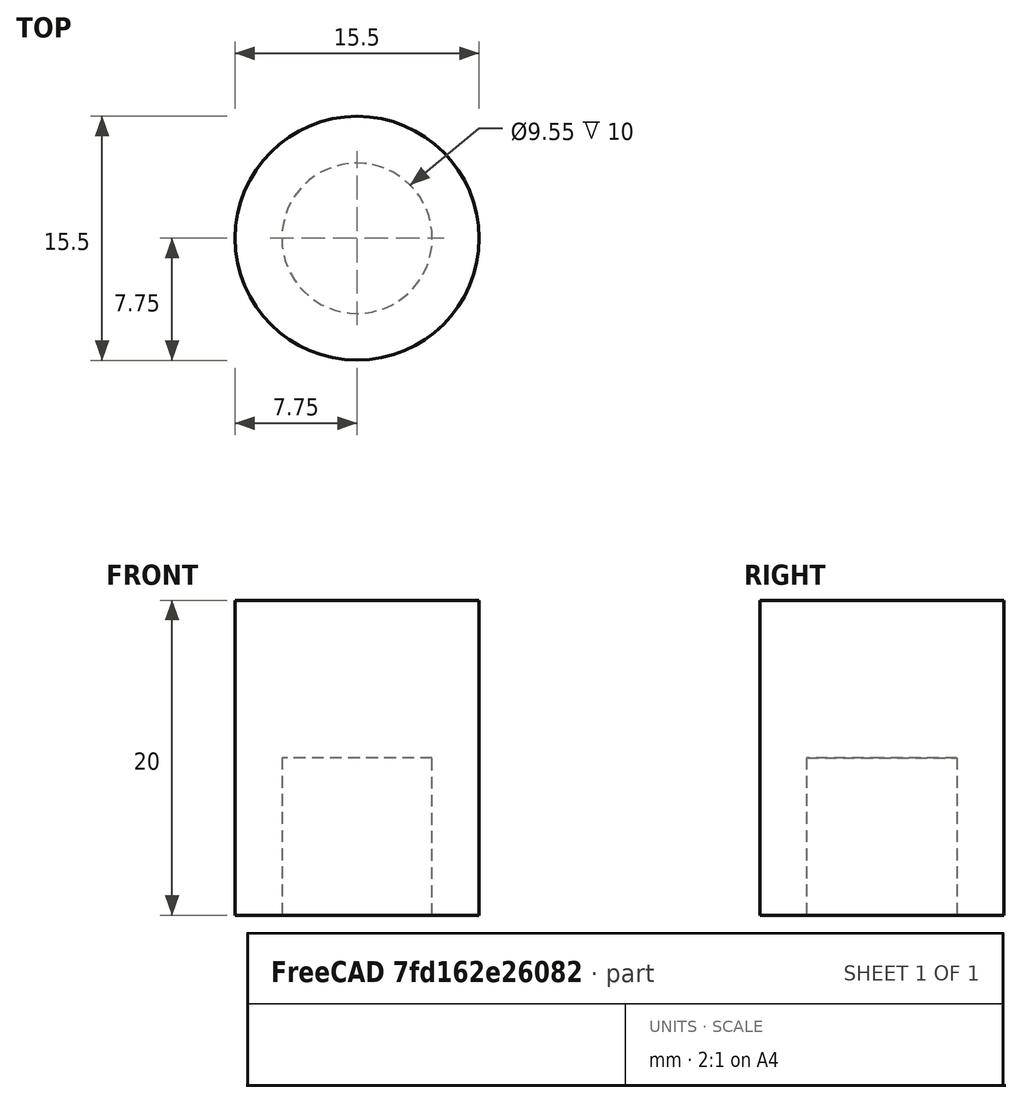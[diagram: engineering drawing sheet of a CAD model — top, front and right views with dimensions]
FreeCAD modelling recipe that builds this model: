
FCSTD DOCUMENT  (FreeCAD 0.19R24291 (Git))
Label: CementSample
License: All rights reserved
LicenseURL: http://en.wikipedia.org/wiki/All_rights_reserved
objects: TechDraw::DrawViewDimension×4, Sketcher::SketchObject×2, TechDraw::DrawProjGroupItem×2, PartDesign::Pad×1, PartDesign::Pocket×1, PartDesign::Body×1, TechDraw::DrawSVGTemplate×1, TechDraw::DrawProjGroup×1, TechDraw::DrawViewSection×1, TechDraw::DrawPage×1
note: 7 computed .brp shape members not serialized (recipe doc carries the construction recipe); baked Part::Feature solids carry a one-line shape summary decoded from their .brp

FEATURE [Sketcher::SketchObject] Sketch
  FullyConstrained = true
  MapMode = 5
  Support = -> [XY_Plane]
  sketch-geometry (1):
    g0: Circle CenterX=0 CenterY=0 CenterZ=0 NormalX=0 NormalY=0 NormalZ=1 AngleXU=0 Radius=7.745
  constraints (2):
    c: Coincident(g0,g-1)
    c: Diameter(g0) = 15.49
FEATURE [PartDesign::Pad] Pad
  Direction = (1,1,1)
  Length = 20
  Length2 = 100
  Profile = -> Sketch
  Type = 0
FEATURE [Sketcher::SketchObject] Sketch001
  FullyConstrained = true
  MapMode = 5
  Placement = pos=(0,0,0) rot=(1,0,0;3.14159rad)
  Support = -> [Pad]
  sketch-geometry (1):
    g0: Circle CenterX=0 CenterY=0 CenterZ=0 NormalX=0 NormalY=0 NormalZ=1 AngleXU=0 Radius=4.775
  constraints (2):
    c: Coincident(g0,g-1)
    c: Diameter(g0) = 9.55
FEATURE [PartDesign::Pocket] Pocket
  BaseFeature = -> Pad
  Length = 10
  Length2 = 100
  Profile = -> Sketch001
  Type = 0
FEATURE [PartDesign::Body] Body
  Group = -> [Sketch,Pad,Sketch001,Pocket]
  Origin = -> Origin
  Tip = -> Pocket
FEATURE [TechDraw::DrawSVGTemplate] Template
  EditableTexts = Designed_by_Name=Designed by Name; Drawing_number=Drawing number; FC-Date=Date; FC-SC=Scale; FC-SH=Sheet; FC-Title=Title; Subtitle=Subtitle; Weight=Weight
  Height = 210
  Orientation = 1
  Width = 297
FEATURE [TechDraw::DrawProjGroupItem] ProjItem  label="Front"
  CoarseView = false
  Direction = (0,1,0)
  Focus = 100
  HardHidden = false
  IsoCount = 0
  IsoHidden = false
  IsoVisible = false
  LockPosition = true
  Perspective = false
  Rotation = 0
  RotationVector = (1,0,0)
  Scale = 2
  ScaleType = 2
  SeamHidden = false
  SeamVisible = true
  SmoothHidden = false
  SmoothVisible = true
  Source = -> [Pocket]
  Type = 0
  X = 0
  XDirection = (1,0,0)
  Y = 0
FEATURE [TechDraw::DrawProjGroupItem] ProjItem001  label="Top"
  CoarseView = false
  Direction = (0,0,-1)
  Focus = 100
  HardHidden = false
  IsoCount = 0
  IsoHidden = false
  IsoVisible = false
  LockPosition = false
  Perspective = false
  Rotation = 0
  RotationVector = (1,0,0)
  Scale = 2
  ScaleType = 2
  SeamHidden = false
  SeamVisible = true
  SmoothHidden = false
  SmoothVisible = true
  Source = -> [Pocket]
  Type = 4
  X = 0
  XDirection = (1,0,0)
  Y = -59.51
FEATURE [TechDraw::DrawProjGroup] ProjGroup
  Anchor = -> ProjItem
  AutoDistribute = true
  LockPosition = false
  ProjectionType = 0
  Rotation = 0
  Scale = 2
  ScaleType = 2
  Source = -> [Pocket]
  Views = -> [ProjItem,ProjItem001]
  X = 68.186
  Y = 152.343
  spacingX = 15
  spacingY = 15
FEATURE [TechDraw::DrawViewSection] SectionView  label="Section  - "
  BaseView = -> ProjItem
  CoarseView = false
  CutSurfaceDisplay = 2
  Direction = (-1,0,0)
  FileGeomPattern = C:/Program Files/FreeCAD 0.19/data/Mod/TechDraw/PAT/FCPAT.pat
  FileHatchPattern = C:/Program Files/FreeCAD 0.19/data/Mod/TechDraw/Patterns/simple.svg
  Focus = 100
  FuseBeforeCut = false
  HardHidden = false
  HatchScale = 1
  IsoCount = 0
  IsoHidden = false
  IsoVisible = false
  LockPosition = false
  NameGeomPattern = Diamond
  Perspective = false
  Rotation = 0
  Scale = 2
  ScaleType = 0
  SeamHidden = false
  SeamVisible = true
  SectionDirection = 0
  SectionNormal = (-1,0,0)
  SectionOrigin = (0,0,10)
  SmoothHidden = false
  SmoothVisible = true
  Source = -> [Pocket]
  X = 111.456
  XDirection = (0,1,0)
  Y = 152.077
FEATURE [TechDraw::DrawViewDimension] Dimension
  Arbitrary = false
  ArbitraryTolerances = false
  EqualTolerance = true
  FormatSpec = %.2f
  FormatSpecOverTolerance = %+.2f
  FormatSpecUnderTolerance = %+.2f
  Inverted = false
  LockPosition = false
  MeasureType = 1
  OverTolerance = 0
  References2D = -> [ProjItem]
  Rotation = 0
  ScaleType = 0
  TheoreticalExact = false
  Type = 2
  UnderTolerance = 0
  X = -24.2365
  Y = 0.514501
FEATURE [TechDraw::DrawViewDimension] Dimension001
  Arbitrary = false
  ArbitraryTolerances = false
  EqualTolerance = true
  FormatSpec = ⌀%.2f
  FormatSpecOverTolerance = %+.2f
  FormatSpecUnderTolerance = %+.2f
  Inverted = false
  LockPosition = false
  MeasureType = 1
  OverTolerance = 0
  References2D = -> [ProjItem001]
  Rotation = 0
  ScaleType = 0
  TheoreticalExact = false
  Type = 5
  UnderTolerance = 0
  X = -24.6288
  Y = 16.7416
FEATURE [TechDraw::DrawViewDimension] Dimension002
  Arbitrary = false
  ArbitraryTolerances = false
  EqualTolerance = true
  FormatSpec = ⌀%.2f
  FormatSpecOverTolerance = %+.2f
  FormatSpecUnderTolerance = %+.2f
  Inverted = false
  LockPosition = false
  MeasureType = 1
  OverTolerance = 0
  References2D = -> [ProjItem001]
  Rotation = 0
  ScaleType = 0
  TheoreticalExact = false
  Type = 5
  UnderTolerance = 0
  X = -24.9533
  Y = -4.88776
FEATURE [TechDraw::DrawViewDimension] Dimension003
  Arbitrary = false
  ArbitraryTolerances = false
  EqualTolerance = true
  FormatSpec = %.2f
  FormatSpecOverTolerance = %+.2f
  FormatSpecUnderTolerance = %+.2f
  Inverted = false
  LockPosition = false
  MeasureType = 1
  OverTolerance = 0
  References2D = -> [SectionView]
  Rotation = 0
  ScaleType = 0
  TheoreticalExact = false
  Type = 2
  UnderTolerance = 0
  X = 28.072
  Y = 7.942
FEATURE [TechDraw::DrawPage] Page
  KeepUpdated = true
  NextBalloonIndex = 1
  ProjectionType = 0
  Template = -> Template
  Views = -> [ProjGroup,SectionView,Dimension,Dimension001,Dimension002,Dimension003]
